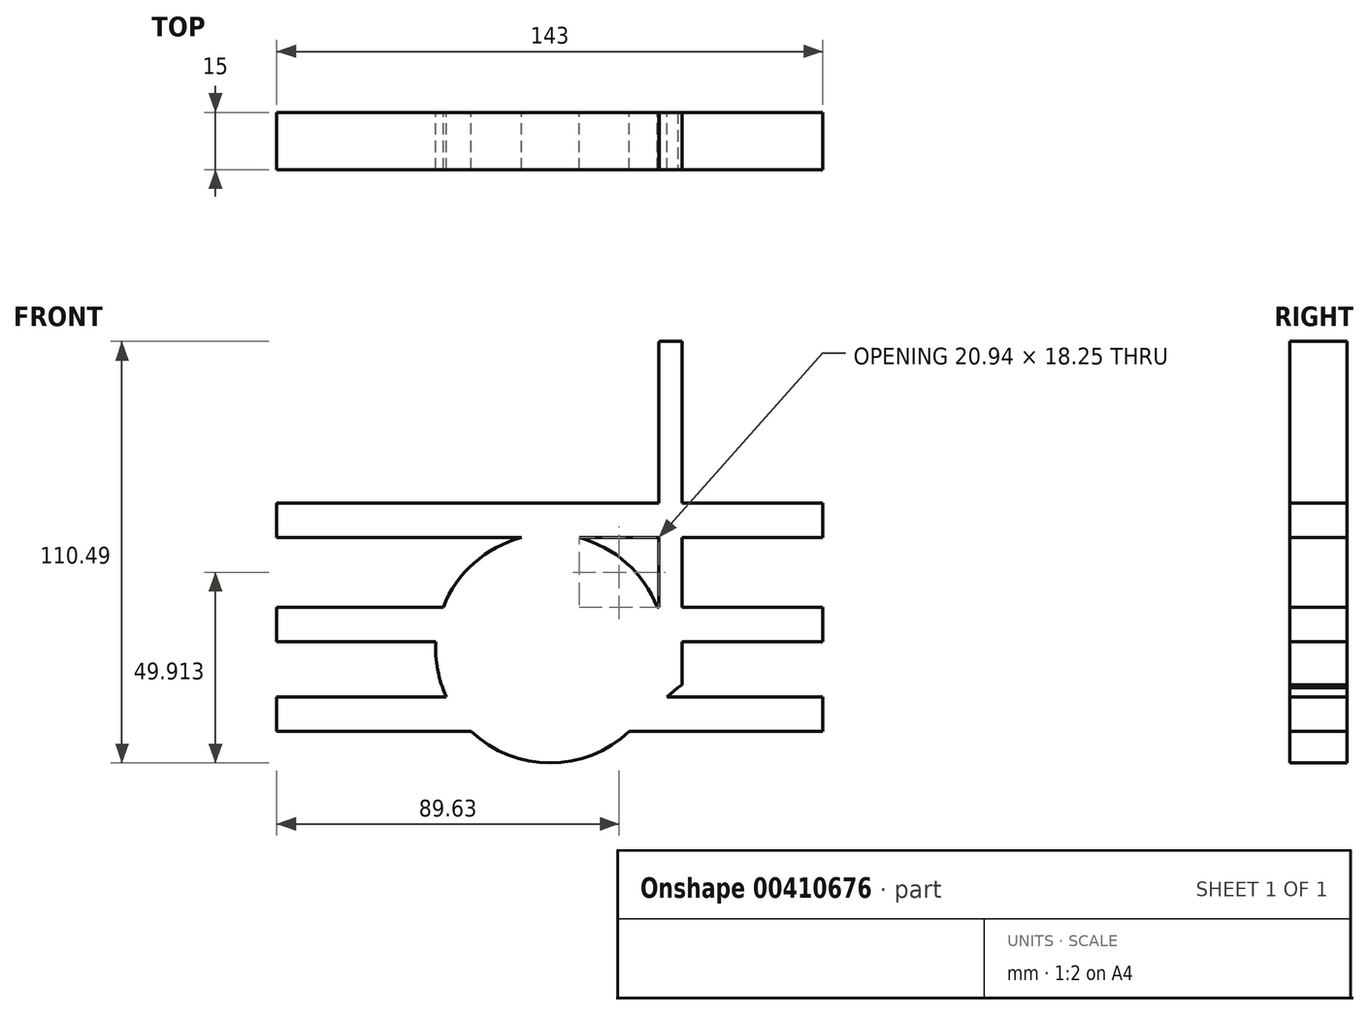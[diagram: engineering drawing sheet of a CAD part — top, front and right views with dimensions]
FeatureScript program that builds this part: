
annotation { "Feature Type Name" : "Feature", "Feature Type Description" : "" }
export const myFeature = defineFeature(function(context is Context, id is Id, definition is map)
    precondition{}
    {
        {
            var Q0;
            Q0=qCreatedBy(makeId("Front.planeOp"),FACE);
            var sketch = newSketch(context, id + "F0", { "sketchPlane" : qUnion([Q0])});
            skCircle(sketch, "E0", {"center": v(0, -38.04) * mm, "radius": 30 * mm});
            skLineSegment(sketch, "E1", {"start": v(28.48, -28.62) * mm, "end": v(28.48, 42.2) * mm});
            skLineSegment(sketch, "E2", {"start": v(28.48, -47.46) * mm, "end": v(34.47, -47.46) * mm});
            skLineSegment(sketch, "E3", {"start": v(34.47, -47.46) * mm, "end": v(34.47, 42.2) * mm});
            skLineSegment(sketch, "E4", {"start": v(34.47, 42.2) * mm, "end": v(28.48, 42.2) * mm});
            skPoint(sketch, "E5", {"position": v(23.64, -56.5) * mm});
            skLineSegment(sketch, "E6", {"start": v(34.47, -47.46) * mm, "end": v(23.64, -56.5) * mm});
            skSolve(sketch);
        }
        {
            var Q0;
            Q0 = qSketchRegion(id + "F0", true);
            extrude(context, id + "F1", {"entities" : qUnion([Q0]), "depth" : 15 * mm});
        }
        {
            var Q0;
            Q0=qCreatedBy(makeId("Front.planeOp"),FACE);
            var sketch = newSketch(context, id + "F2", { "sketchPlane" : qUnion([Q0])});
            skLineSegment(sketch, "E7.bottom", {"start": v(71.38, 0) * mm, "end": v(-71.62, 0) * mm});
            skLineSegment(sketch, "E7.top", {"start": v(71.38, -9) * mm, "end": v(-71.62, -9) * mm});
            skLineSegment(sketch, "E7.left", {"start": v(71.38, 0) * mm, "end": v(71.38, -9) * mm});
            skLineSegment(sketch, "E7.right", {"start": v(-71.62, 0) * mm, "end": v(-71.62, -9) * mm});
            skLineSegment(sketch, "E8.bottom", {"start": v(71.38, -27.25) * mm, "end": v(-71.62, -27.25) * mm});
            skLineSegment(sketch, "E8.top", {"start": v(71.38, -36.25) * mm, "end": v(-71.62, -36.25) * mm});
            skLineSegment(sketch, "E8.left", {"start": v(71.38, -27.25) * mm, "end": v(71.38, -36.25) * mm});
            skLineSegment(sketch, "E8.right", {"start": v(-71.62, -27.25) * mm, "end": v(-71.62, -36.25) * mm});
            skPoint(sketch, "E9.firstSnap0", {"position": v(71.38, -31.75) * mm});
            skLineSegment(sketch, "E9.bottom", {"start": v(71.38, -50.73) * mm, "end": v(-71.62, -50.73) * mm});
            skLineSegment(sketch, "E9.top", {"start": v(71.38, -59.73) * mm, "end": v(-71.62, -59.73) * mm});
            skLineSegment(sketch, "E9.left", {"start": v(71.38, -50.73) * mm, "end": v(71.38, -59.73) * mm});
            skLineSegment(sketch, "E9.right", {"start": v(-71.62, -50.73) * mm, "end": v(-71.62, -59.73) * mm});
            skSolve(sketch);
        }
        {
            var Q0;
            Q0 = qSketchRegion(id + "F2", true);
            extrude(context, id + "F3", {"entities" : qUnion([Q0]), "operationType" : NewBodyOperationType.ADD, "depth" : 15 * mm});
        }
        {
            var Q0;
            Q0=qCreatedBy(makeId("Front.planeOp"),FACE);
            var sketch = newSketch(context, id + "F4", { "sketchPlane" : qUnion([Q0])});
            skPoint(sketch, "E10", {"position": v(0, -8.04) * mm});
            skPoint(sketch, "E11", {"position": v(0, -38.04) * mm});
            skCircle(sketch, "E12", {"center": v(0, -38.04) * mm, "radius": 30 * mm});
            skPoint(sketch, "E13", {"position": v(34.47, -47.55) * mm});
            skPoint(sketch, "E14", {"position": v(24.91, -54.75) * mm});
            skLineSegment(sketch, "E15", {"start": v(24.91, -54.75) * mm, "end": v(34.47, -47.55) * mm});
            skLineSegment(sketch, "E16", {"start": v(34.47, -47.55) * mm, "end": v(34.47, 42.45) * mm});
            skLineSegment(sketch, "E17", {"start": v(28.53, 42.45) * mm, "end": v(34.47, 42.45) * mm});
            skLineSegment(sketch, "E18", {"start": v(28.53, 42.45) * mm, "end": v(28.53, -28.76) * mm});
            skSolve(sketch);
        }
        {
            var Q0;
            Q0 = qSketchRegion(id + "F4", true);
            extrude(context, id + "F5", {"entities" : qUnion([Q0]), "operationType" : NewBodyOperationType.ADD, "depth" : 15 * mm});
        }
    });
